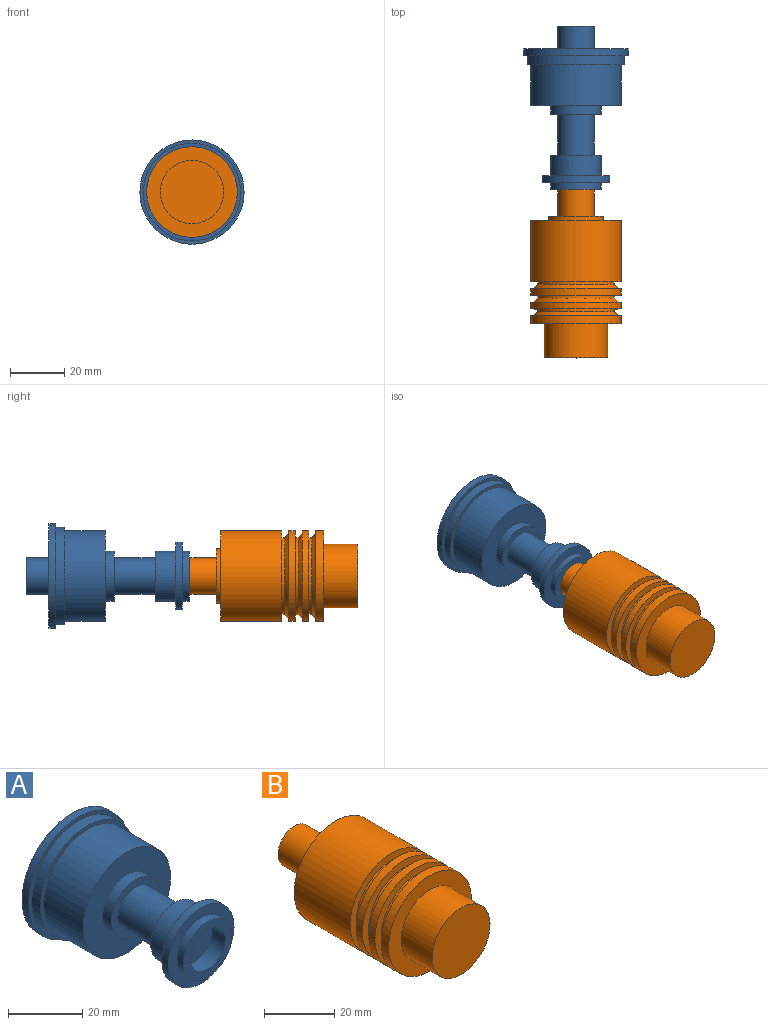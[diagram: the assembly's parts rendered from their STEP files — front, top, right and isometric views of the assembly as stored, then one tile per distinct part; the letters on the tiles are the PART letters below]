
ASSEMBLY  parts=2 mates=1
PART A: 25 faces, bbox 38.3x60x38.3 mm
  f0: plane 18.4x18.4mm, normal (0,-1,0), area 127mm2, adj f20,f21
  f1: plane 13.4x13.4mm, normal (0,1,0), area 71.6mm2, adj f2,f24
  f2: cylinder r=6.7mm len=13.4mm, axis (0,1,0), area 564.1mm2, adj f1,f3
  f3: plane 18.4x18.4mm, normal (0,1,0), area 124.9mm2, adj f2,f4
  f4: cylinder r=9.2mm len=18.4mm, axis (0,1,0), area 289mm2, adj f3,f5
  f5: plane 38.3x38.3mm, normal (0,1,0), area 886.2mm2, adj f4,f6
  f6: cylinder r=19.15mm len=38.3mm, axis (0,1,0), area 300.8mm2, adj f5,f7
  f7: plane 38.3x38.3mm, normal (0,-1,0), area 145.5mm2, adj f6,f8
  f8: cylinder r=17.9mm len=35.8mm, axis (0,1,0), area 371.1mm2, adj f7,f9
  f9: plane 35.8x35.8mm, normal (0,-1,0), area 135.7mm2, adj f8,f10
  f10: cylinder r=16.65mm len=33.3mm, axis (0,1,0), area 1569.2mm2, adj f9,f11
  f11: plane 33.3x33.3mm, normal (0,-1,0), area 605mm2, adj f10,f12
  f12: cylinder r=9.2mm len=18.4mm, axis (0,1,0), area 190.8mm2, adj f11,f13
  f13: plane 18.4x18.4mm, normal (0,-1,0), area 124.9mm2, adj f12,f14
  f14: cylinder r=6.7mm len=15mm, axis (0,1,0), area 631.5mm2, adj f13,f15
  f15: plane 18.4x18.4mm, normal (0,1,0), area 124.9mm2, adj f14,f16
  f16: cylinder r=9.2mm len=18.4mm, axis (0,1,0), area 433.5mm2, adj f15,f17
  f17: plane 25x25mm, normal (0,1,0), area 225mm2, adj f16,f18
  f18: cylinder r=12.5mm len=25mm, axis (0,1,0), area 196.3mm2, adj f17,f19
  f19: plane 25x25mm, normal (0,-1,0), area 225mm2, adj f18,f20
  f20: cylinder r=9.2mm len=18.4mm, axis (0,1,0), area 144.5mm2, adj f0,f19
  f21: cylinder r=6.65mm len=13.3mm, axis (0,-1,0), area 208.9mm2, adj f0,f22
  f22: plane 13.3x13.3mm, normal (0,-1,0), area 138.9mm2, adj f21
  f23: plane 9.4x9.4mm, normal (0,1,0), area 69.4mm2, adj f24
  f24: cylinder r=4.7mm len=10.9mm, axis (0,1,0), area 321.9mm2, adj f1,f23
PART B: 24 faces, bbox 33.3x67x33.3 mm
  f0: plane 33.3x33.3mm, normal (0,-1,0), area 444.5mm2, adj f14,f18
  f1: plane 33.3x33.3mm, normal (0,1,0), area 559.9mm2, adj f2,f20
  f2: cylinder r=16.65mm len=33.3mm, axis (0,1,0), area 2353.8mm2, adj f1,f3
  f3: plane 33.3x33.3mm, normal (0,-1,0), area 241.9mm2, adj f2,f4
  f4: cylinder r=14.15mm len=28.3mm, axis (0,1,0), area 88.9mm2, adj f3,f15
  f5: plane 33.3x33.3mm, normal (0,1,0), area 101.5mm2, adj f6,f15
  f6: cylinder r=16.65mm len=33.3mm, axis (0,1,0), area 261.5mm2, adj f5,f7
  f7: plane 33.3x33.3mm, normal (0,-1,0), area 241.9mm2, adj f6,f8
  f8: cylinder r=14.15mm len=28.3mm, axis (0,1,0), area 88.9mm2, adj f7,f16
  f9: plane 33.3x33.3mm, normal (0,1,0), area 101.5mm2, adj f10,f16
  f10: cylinder r=16.65mm len=33.3mm, axis (0,1,0), area 261.5mm2, adj f9,f11
  f11: plane 33.3x33.3mm, normal (0,-1,0), area 241.9mm2, adj f10,f12
  f12: cylinder r=14.15mm len=28.3mm, axis (0,1,0), area 88.9mm2, adj f11,f17
  f13: plane 33.3x33.3mm, normal (0,1,0), area 101.5mm2, adj f14,f17
  f14: cylinder r=16.65mm len=33.3mm, axis (0,1,0), area 313.8mm2, adj f0,f13
  f15: cone r=14.15mm half-angle=45deg, axis (0,-1,0), area 198.6mm2, adj f4,f5
  f16: cone r=14.15mm half-angle=45deg, axis (0,-1,0), area 198.6mm2, adj f8,f9
  f17: cone r=14.15mm half-angle=45deg, axis (0,-1,0), area 198.6mm2, adj f12,f13
  f18: cylinder r=11.65mm len=23.3mm, axis (0,1,0), area 915mm2, adj f0,f19
  f19: plane 23.3x23.3mm, normal (0,-1,0), area 426.4mm2, adj f18
  f20: cylinder r=9.95mm len=19.9mm, axis (0,-1,0), area 93.8mm2, adj f1,f21
  f21: plane 19.9x19.9mm, normal (0,1,0), area 172.1mm2, adj f20,f22
  f22: cylinder r=6.65mm len=15mm, axis (0,-1,0), area 626.7mm2, adj f21,f23
  f23: plane 13.3x13.3mm, normal (0,1,0), area 138.9mm2, adj f22
PLACE A t=(-14.69,53.83,7.59)mm
PLACE B t=(-14.69,-6.67,7.59)mm
MATE fastened A.f21 <-> B.f22  axis (0,-1,0) through (-14.69,28.83,7.59)mm
